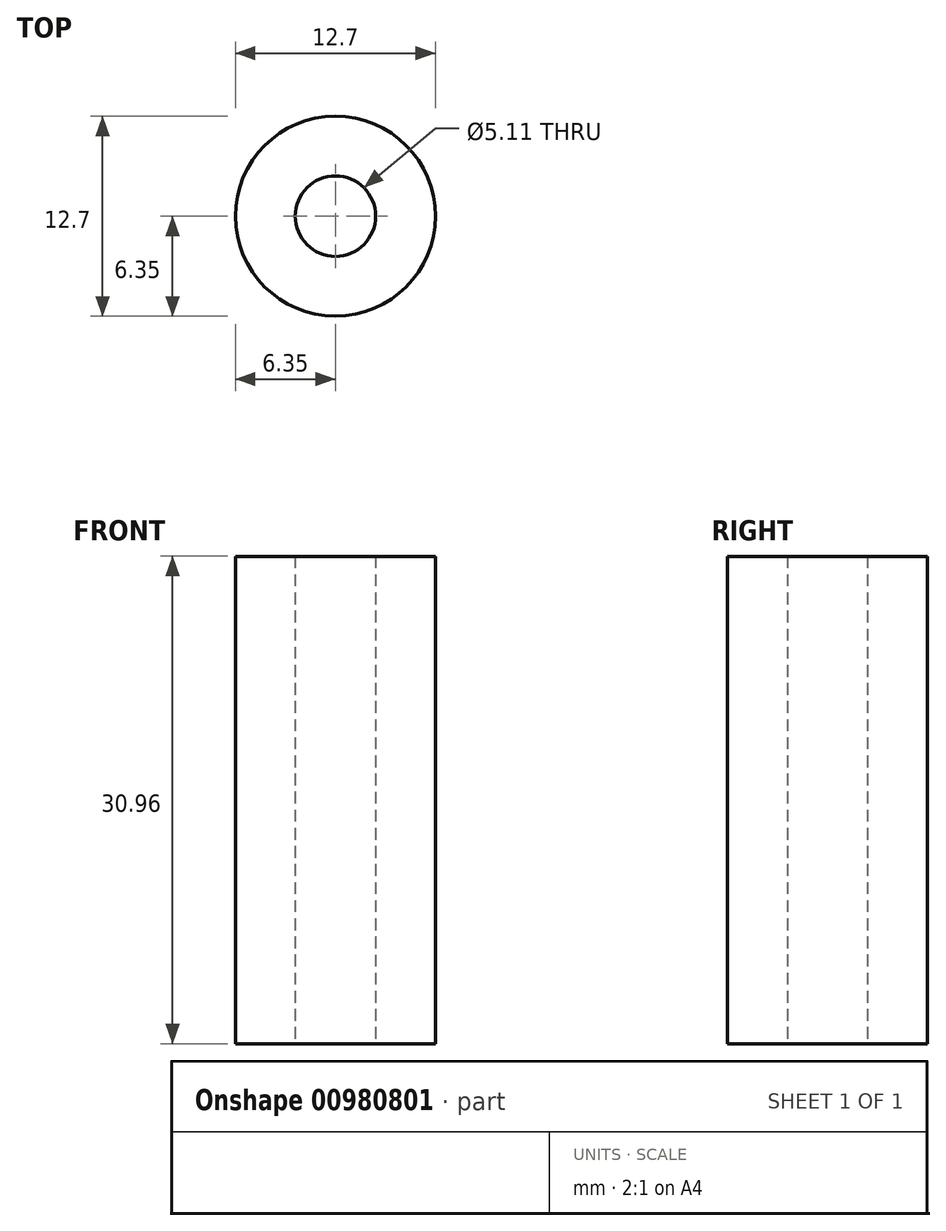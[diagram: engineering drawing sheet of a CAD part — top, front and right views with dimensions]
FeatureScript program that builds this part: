
annotation { "Feature Type Name" : "Feature", "Feature Type Description" : "" }
export const myFeature = defineFeature(function(context is Context, id is Id, definition is map)
    precondition{}
    {
        {
            var Q0;
            Q0=qCreatedBy(makeId("Top.planeOp"),FACE);
            var sketch = newSketch(context, id + "F0", { "sketchPlane" : qUnion([Q0])});
            skCircle(sketch, "E0", {"center": v(0, 0) * mm, "radius": 2.55 * mm});
            skCircle(sketch, "E1", {"center": v(0, 0) * mm, "radius": 6.35 * mm});
            skSolve(sketch);
        }
        {
            var Q0;
            Q0 = qSketchRegion(id + "F0", true);
            extrude(context, id + "F1", {"entities" : qUnion([Q0]), "depth" : 30.96 * mm, "offsetDistance" : 25.4 * mm});
        }
    });
